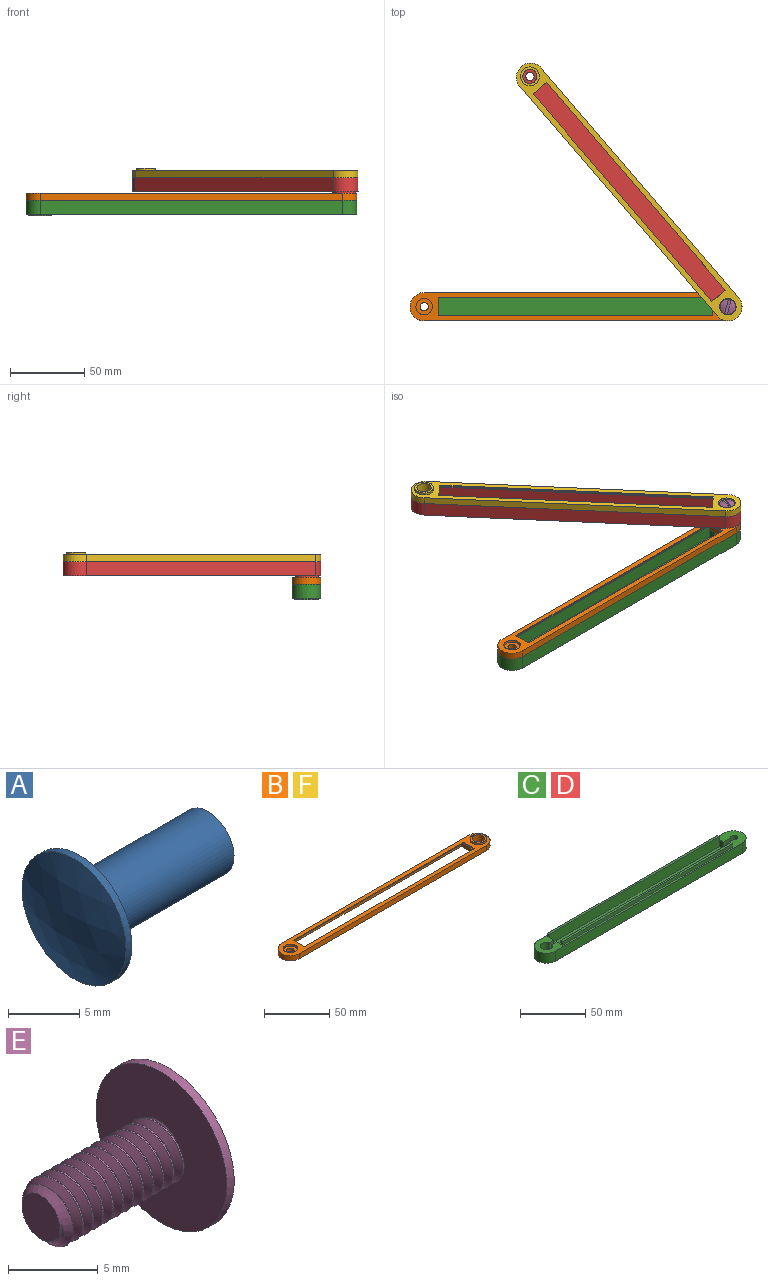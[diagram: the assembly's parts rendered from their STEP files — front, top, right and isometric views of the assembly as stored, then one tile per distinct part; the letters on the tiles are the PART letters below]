
ASSEMBLY  parts=6 mates=11
PART A: 11 faces, bbox 14.9x10.7x10.7 mm
  f0: cylinder r=5.16mm len=10.32mm, axis (1,0,0), area 18.7mm2, adj f1,f10
  f1: sphere r=13.68mm, area 86.8mm2, adj f0
  f2: cone r=2.08mm half-angle=45deg, axis (1,0,0), area 4.3mm2, adj f5,f6,f7,f8
  f3: cylinder r=2.58mm len=12.7mm, axis (1,0,0), area 205.8mm2, adj f8,f10
  f4: cylinder r=2.08mm len=7.94mm, axis (1,0,0), area 13mm2, adj f5,f6,f8,f9
  f5: bspline ~8.63x4.17mm, area 65.1mm2, adj f2,f4,f7,f9
  f6: bspline ~8.24x4.16mm, area 66.3mm2, adj f2,f4,f7,f9
  f7: cylinder r=1.57mm len=7.42mm, axis (1,0,0), area 9.1mm2, adj f2,f5,f6,f9
  f8: plane 5.16x5.16mm, normal (1,0,0), area 7.3mm2, adj f2,f3,f4
  f9: plane 4x3.98mm, normal (1,0,0), area 10.6mm2, adj f4,f5,f6,f7
  f10: plane 10.32x10.32mm, normal (1,0,0), area 62.7mm2, adj f0,f3
PART B: 25 faces, bbox 222.3x19.1x6.4 mm
  f0: cylinder r=2.78mm len=5.56mm, axis (0,0,-1), area 55.4mm2, adj f11,f23
  f1: plane 16x3.18mm, normal (-1,0,0), area 50.8mm2, adj f4,f10,f11,f18
  f2: plane 16x3.18mm, normal (1,0,0), area 50.8mm2, adj f4,f10,f11,f17
  f3: plane 12x0.79mm, normal (-1,0,0), area 9.5mm2, adj f12,f13,f14,f15
  f4: plane 185.74x3.97mm, normal (0,1,0), area 732.1mm2, adj f1,f2,f11,f12,f16,f17,f18,f19
  f5: plane 12x0.79mm, normal (1,0,0), area 9.5mm2, adj f12,f13,f14,f15
  f6: cylinder r=9.53mm len=19.05mm, axis (0,0,-1), area 142.5mm2, adj f7,f9,f11,f15
  f7: plane 203.2x4.76mm, normal (0,-1,0), area 967.7mm2, adj f6,f8,f11,f15
  f8: cylinder r=9.53mm len=19.05mm, axis (0,0,-1), area 142.5mm2, adj f7,f9,f11,f15
  f9: plane 203.2x4.76mm, normal (0,1,0), area 967.7mm2, adj f6,f8,f11,f15
  f10: plane 185.74x3.97mm, normal (0,-1,0), area 732.1mm2, adj f1,f2,f11,f12,f16,f17,f18,f19
  f11: plane 222.25x19.05mm, normal (0,0,-1), area 1114.1mm2, adj f0,f1,f2,f4,f6,f7,f8,f9
  f12: plane 185.74x16mm, normal (0,0,-1), area 762mm2, adj f3,f4,f5,f10,f13,f14,f16,f19
  f13: plane 184.15x0.79mm, normal (0,-1,0), area 146.2mm2, adj f3,f5,f12,f15
  f14: plane 184.15x0.79mm, normal (0,1,0), area 146.2mm2, adj f3,f5,f12,f15
  f15: plane 222.25x19.05mm, normal (0,0,1), area 1722.5mm2, adj f3,f5,f6,f7,f8,f9,f13,f14
  f16: plane 16x0.79mm, normal (1,0,0), area 12.7mm2, adj f4,f10,f12,f17
  f17: plane 16x0.79mm, normal (0,0,1), area 12.7mm2, adj f2,f4,f10,f16
  f18: plane 16x0.79mm, normal (0,0,1), area 12.7mm2, adj f1,f4,f10,f19
  f19: plane 16x0.79mm, normal (-1,0,0), area 12.7mm2, adj f4,f10,f12,f18
  f20: cylinder r=6.35mm len=12.7mm, axis (0,0,-1), area 63.3mm2, adj f15,f21
  f21: plane 12.7x12.7mm, normal (0,0,1), area 55.4mm2, adj f20,f24
  f22: cylinder r=5.56mm len=11.11mm, axis (0,0,1), area 55.4mm2, adj f15,f23
  f23: plane 11.11x11.11mm, normal (0,0,1), area 72.7mm2, adj f0,f22
  f24: cylinder r=4.76mm len=9.53mm, axis (0,0,1), area 190mm2, adj f11,f21
PART C: 33 faces, bbox 222.3x19.1x13.5 mm
  f0: cylinder r=2.78mm len=7.94mm, axis (0,0,1), area 117.1mm2, adj f1,f20,f21,f25,f29
  f1: plane 222.25x19.05mm, normal (0,0,1), area 1074.4mm2, adj f0,f2,f3,f4,f5,f7,f9,f10
  f2: plane 203.2x9.53mm, normal (0,-1,0), area 1935.5mm2, adj f1,f3,f5,f6
  f3: cylinder r=9.53mm len=19.05mm, axis (0,0,-1), area 285mm2, adj f1,f2,f4,f6
  f4: plane 203.2x9.53mm, normal (0,1,0), area 1935.5mm2, adj f1,f3,f5,f6
  f5: cylinder r=9.53mm len=19.05mm, axis (0,0,-1), area 285mm2, adj f1,f2,f4,f6
  f6: plane 222.25x19.05mm, normal (0,0,-1), area 3861.1mm2, adj f2,f3,f4,f5,f26,f28
  f7: plane 3.18x2mm, normal (-1,0,0), area 6.4mm2, adj f1,f8,f10,f11
  f8: plane 184.15x9.53mm, normal (0,-1,0), area 1754mm2, adj f7,f9,f11,f22,f23,f25
  f9: plane 3.18x2mm, normal (1,0,0), area 6.4mm2, adj f1,f8,f10,f11
  f10: plane 184.15x3.18mm, normal (0,1,0), area 584.7mm2, adj f1,f7,f9,f11
  f11: plane 184.15x2mm, normal (0,0,1), area 368.3mm2, adj f7,f8,f9,f10
  f12: plane 184.15x9.53mm, normal (0,1,0), area 1754mm2, adj f13,f15,f16,f18,f19,f25
  f13: plane 3.18x2mm, normal (-1,0,0), area 6.4mm2, adj f1,f12,f14,f16
  f14: plane 184.15x3.18mm, normal (0,-1,0), area 584.7mm2, adj f1,f13,f15,f16
  f15: plane 3.18x2mm, normal (1,0,0), area 6.4mm2, adj f1,f12,f14,f16
  f16: plane 184.15x2mm, normal (0,0,1), area 368.3mm2, adj f12,f13,f14,f15
  f17: plane 6.35x5.04mm, normal (0,1,0), area 32mm2, adj f1,f18,f25,f32
  f18: plane 6.35x4.41mm, normal (1,0,0), area 28mm2, adj f1,f12,f17,f25
  f19: plane 6.35x4.41mm, normal (-1,0,0), area 28mm2, adj f1,f12,f20,f25
  f20: plane 8x6.35mm, normal (0,1,0), area 50.8mm2, adj f0,f1,f19,f25
  f21: plane 8x6.35mm, normal (0,-1,0), area 50.8mm2, adj f0,f1,f22,f25
  f22: plane 6.35x4.41mm, normal (-1,0,0), area 28mm2, adj f1,f8,f21,f25
  f23: plane 6.35x4.41mm, normal (1,0,0), area 28mm2, adj f1,f8,f24,f25
  f24: plane 6.35x5.04mm, normal (0,-1,0), area 32mm2, adj f1,f23,f25,f32
  f25: plane 197.18x12mm, normal (0,0,1), area 2249.5mm2, adj f0,f8,f12,f17,f18,f19,f20,f21
  f26: cylinder r=7.94mm len=15.88mm, axis (0,0,1), area 39.6mm2, adj f6,f27
  f27: plane 15.88x15.88mm, normal (0,0,-1), area 71.3mm2, adj f26,f30
  f28: cylinder r=5.56mm len=11.11mm, axis (0,0,-1), area 55.4mm2, adj f6,f29
  f29: plane 11.11x11.11mm, normal (0,0,-1), area 72.7mm2, adj f0,f28
  f30: cylinder r=6.35mm len=12.7mm, axis (0,0,-1), area 63.3mm2, adj f27,f31
  f31: plane 12.7x12.7mm, normal (0,0,-1), area 55.4mm2, adj f30,f32
  f32: cylinder r=4.76mm len=9.53mm, axis (0,0,-1), area 240.7mm2, adj f1,f17,f24,f25,f31
PART D: same geometry as C
PART E: 13 faces, bbox 11.6x10.6x10.6 mm
  f0: cone r=2.08mm half-angle=45deg, axis (1,0,0), area 5.1mm2, adj f1,f9,f10,f11,f12
  f1: cylinder r=2.08mm len=8.93mm, axis (-1,0,0), area 14.6mm2, adj f0,f5,f10,f11
  f2: cylinder r=5.16mm len=10.32mm, axis (-1,0,0), area 18.7mm2, adj f3,f4,f5,f8
  f3: sphere r=13.68mm, area 33.1mm2, adj f2,f7
  f4: sphere r=13.68mm, area 33.1mm2, adj f2,f6
  f5: plane 10.62x10.62mm, normal (-1,0,0), area 73.1mm2, adj f1,f2,f10,f11,f12
  f6: plane 10.29x1.12mm, normal (0,-1,0), area 6.7mm2, adj f4,f8
  f7: plane 10.29x1.12mm, normal (0,1,0), area 6.7mm2, adj f3,f8
  f8: plane 10.32x1.87mm, normal (1,0,0), area 19.2mm2, adj f2,f6,f7
  f9: plane 2.98x2.98mm, normal (-1,0,0), area 7mm2, adj f0
  f10: bspline ~10.04x3.36mm, area 79.1mm2, adj f0,f1,f5,f12
  f11: bspline ~9.92x4.17mm, area 79.1mm2, adj f0,f1,f5,f12
  f12: cylinder r=1.57mm len=9.45mm, axis (1,0,0), area 11.6mm2, adj f0,f5,f10,f11
PART F: same geometry as B
PLACE A rot(axis=(0.71,-0.02,0.71),177.3deg) t=(78.45,-71.32,-63.41)mm
PLACE B rot(axis=(0.32,-0.61,-0.73),0deg) t=(-59.92,-4.68,68.36)mm
PLACE C t=(-59.92,-4.68,68.36)mm fixed
PLACE D rot(axis=(0,0,1),130.7deg) t=(-14.83,-65.03,83.44)mm
PLACE E rot(axis=(-0.62,-0.48,-0.62),129.1deg) t=(78.48,-71.35,-65.79)mm
PLACE F rot(axis=(0,0,1),130.7deg) t=(-14.83,-65.03,83.44)mm
MATE planar D.f1 <-> F.f11  axis (0,0,1) through (-61.22,76.57,-59.44)mm
MATE planar C.f0 <-> A.f7  axis (0,0,-1) through (78.45,-71.32,-82.46)mm
MATE slider F.f0 <-> D.f5  axis (0,0,-1) through (78.45,-71.32,-56.26)mm
MATE cylindrical A.f2 <-> C.f0  axis (0,0,1) through (78.45,-71.32,-76.11)mm
MATE planar E.f5 <-> F.f0  axis (0,0,-1) through (79.72,-69.98,-56.26)mm
MATE cylindrical F.f20 <-> D.f0  axis (0,0,1) through (-54.48,83.35,-56.26)mm
MATE planar B.f11 <-> C.f1  axis (0,0,-1) through (-28.23,-71.32,-74.52)mm
MATE slider B.f20 <-> C.f0  axis (0,0,1) through (78.45,-71.32,-68.17)mm
MATE cylindrical B.f20 <-> D.f5  axis (0,0,-1) through (78.45,-71.32,-68.96)mm
MATE cylindrical A.f2 <-> E.f5  axis (0,0,1) through (78.45,-71.32,-76.11)mm
MATE planar D.f5 <-> B.f20  axis (0,0,-1) through (78.45,-71.32,-68.17)mm
